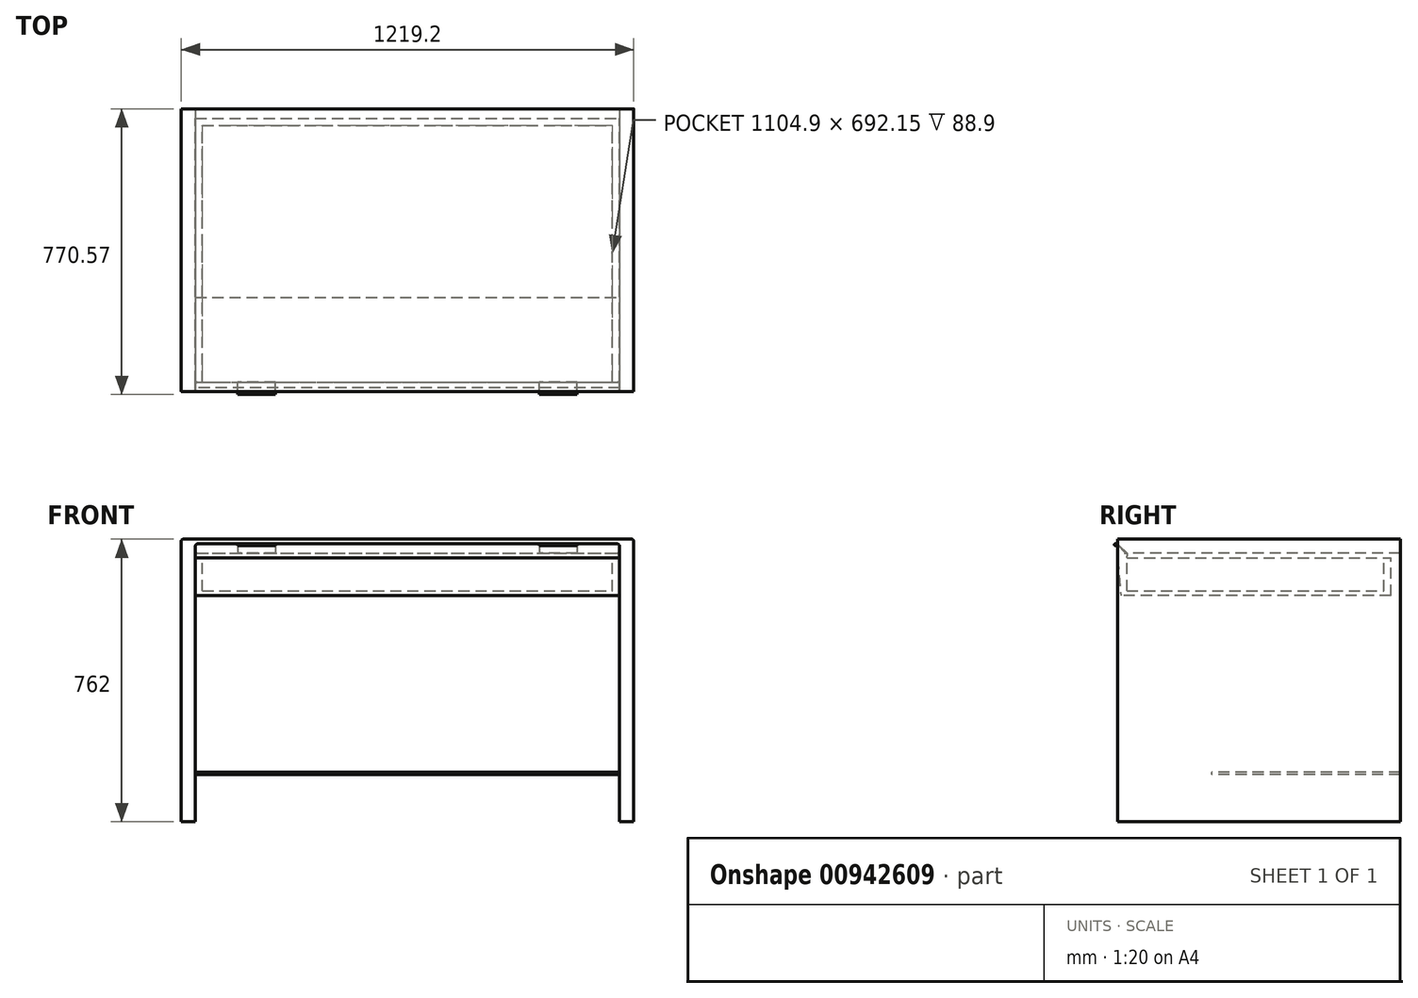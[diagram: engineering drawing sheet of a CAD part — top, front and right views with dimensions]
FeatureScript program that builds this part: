
annotation { "Feature Type Name" : "Feature", "Feature Type Description" : "" }
export const myFeature = defineFeature(function(context is Context, id is Id, definition is map)
    precondition{}
    {
        {
            var Q0;
            Q0=qCreatedBy(makeId("Top.planeOp"),FACE);
            var sketch = newSketch(context, id + "F0", { "sketchPlane" : qUnion([Q0])});
            skLineSegment(sketch, "E0.bottom", {"start": v(-1181.1, 736.46) * mm, "end": v(38.1, 736.46) * mm});
            skLineSegment(sketch, "E0.top", {"start": v(-1181.1, -25.54) * mm, "end": v(38.1, -25.54) * mm});
            skLineSegment(sketch, "E0.left", {"start": v(-1181.1, 736.46) * mm, "end": v(-1181.1, -25.54) * mm});
            skLineSegment(sketch, "E0.right", {"start": v(38.1, 736.46) * mm, "end": v(38.1, -25.54) * mm});
            skLineSegment(sketch, "E1", {"start": v(0, 736.46) * mm, "end": v(0, -25.54) * mm});
            skLineSegment(sketch, "E2", {"start": v(-1143, 736.46) * mm, "end": v(-1143, -25.54) * mm});
            skLineSegment(sketch, "E3", {"start": v(-1143, 228.46) * mm, "end": v(0, 228.46) * mm});
            skLineSegment(sketch, "E4", {"start": v(-1143, -0.14) * mm, "end": v(0, -0.14) * mm});
            skSolve(sketch);
        }
        {
            var Q0;
            {var subQ5=sQuery(id+"F0.wireOp",EDGE,"E4");Q0=makeQuery(id+"F0.imprint","IMPRINT",FACE,{"disambiguationData":[TD([[makeQuery(id+"F0.imprint","IMPRINT",EDGE,{"derivedFrom":subQ5}),-1.0]])]});}
            var Q1;
            {var subQ0=sQuery(id+"F0.wireOp",EDGE,"E3");Q1=makeQuery(id+"F0.imprint","IMPRINT",FACE,{"disambiguationData":[TD([[makeQuery(id+"F0.imprint","IMPRINT",EDGE,{"derivedFrom":subQ0}),-1.0]])]});}
            var Q2;
            {var subQ5=sQuery(id+"F0.wireOp",EDGE,"E3");Q2=makeQuery(id+"F0.imprint","IMPRINT",FACE,{"disambiguationData":[TD([[makeQuery(id+"F0.imprint","IMPRINT",EDGE,{"derivedFrom":subQ5}),1.0]])]});}
            extrude(context, id + "F1", {"entities" : qUnion([Q0, Q1, Q2]), "oppositeDirection" : true, "depth" : 38.1 * mm, "offsetDistance" : 25.4 * mm});
        }
        {
            var Q0;
            {var subQ4=sQuery(id+"F0.wireOp",EDGE,"E0.left");Q0=makeQuery(id+"F0.imprint","IMPRINT",FACE,{"disambiguationData":[TD([[makeQuery(id+"F0.imprint","IMPRINT",EDGE,{"derivedFrom":subQ4}),1.0]])]});}
            var Q1;
            {var subQ4=sQuery(id+"F0.wireOp",EDGE,"E0.right");Q1=makeQuery(id+"F0.imprint","IMPRINT",FACE,{"disambiguationData":[TD([[makeQuery(id+"F0.imprint","IMPRINT",EDGE,{"derivedFrom":subQ4}),-1.0]])]});}
            extrude(context, id + "F2", {"entities" : qUnion([Q0, Q1]), "operationType" : NewBodyOperationType.ADD, "oppositeDirection" : true, "depth" : 762 * mm, "offsetDistance" : 25.4 * mm});
        }
        {
            var Q0;
            Q0=makeQuery(id+"F1.opExtrude","CAP_EDGE",EDGE,{"disambiguationData":[OSD([sQuery(id+"F0.wireOp",EDGE,"E0.top")])],"isStart":false});
            chamfer(context, id + "F3", {"entities" : qUnion([Q0]), "width" : 25.4 * mm, "tangentPropagation" : true});
        }
        {
            var Q0;
            Q0=makeQuery(id+"F3.opChamfer","BLEND_EDGE",EDGE,{"blendedFrom":[makeQuery(id+"F1.opExtrude","CAP_EDGE",EDGE,{"disambiguationData":[OSD([sQuery(id+"F0.wireOp",EDGE,"E0.top")])],"isStart":false}),makeQuery(id+"F2.opExtrude","SWEPT_FACE",FACE,{"disambiguationData":[OSD([sQuery(id+"F0.wireOp",EDGE,"E2")])]})],"blendedInto":[makeQuery(id+"F2.opExtrude","SWEPT_FACE",FACE,{"disambiguationData":[OSD([sQuery(id+"F0.wireOp",EDGE,"E2")])]})]});
            var Q1;
            Q1=makeQuery(id+"F3.opChamfer","BLEND_EDGE",EDGE,{"blendedFrom":[makeQuery(id+"F1.opExtrude","CAP_EDGE",EDGE,{"disambiguationData":[OSD([sQuery(id+"F0.wireOp",EDGE,"E0.top")])],"isStart":false}),makeQuery(id+"F2.opExtrude","SWEPT_FACE",FACE,{"disambiguationData":[OSD([sQuery(id+"F0.wireOp",EDGE,"E1")])]})],"blendedInto":[makeQuery(id+"F2.opExtrude","SWEPT_FACE",FACE,{"disambiguationData":[OSD([sQuery(id+"F0.wireOp",EDGE,"E1")])]})]});
            fillet(context, id + "F4", {"entities" : qUnion([Q0, Q1]), "radius" : 5.08 * mm, "tangentPropagation" : true, "allowEdgeOverflow" : false});
        }
        {
            var Q0;
            {var subQ5=sQuery(id+"F0.wireOp",EDGE,"E4");Q0=makeQuery(id+"F0.imprint","IMPRINT",FACE,{"disambiguationData":[TD([[makeQuery(id+"F0.imprint","IMPRINT",EDGE,{"derivedFrom":subQ5}),-1.0]])]});}
            extrude(context, id + "F5", {"entities" : qUnion([Q0]), "oppositeDirection" : true, "depth" : 152.4 * mm, "offsetDistance" : 25.4 * mm, "hasSecondDirection" : true, "secondDirectionOppositeDirection" : true, "secondDirectionDepth" : 12.7 * mm});
        }
        {
            var Q0;
            Q0=makeQuery(id+"F5.opExtrude","CAP_EDGE",EDGE,{"disambiguationData":[OSD([sQuery(id+"F0.wireOp",EDGE,"E4")])],"isStart":true});
            chamfer(context, id + "F6", {"entities" : qUnion([Q0]), "width" : 25.4 * mm, "tangentPropagation" : true});
        }
        {
            var Q0;
            Q0=makeQuery(id+"F6.opChamfer","BLEND_EDGE",EDGE,{"blendedFrom":[makeQuery(id+"F5.opExtrude","CAP_EDGE",EDGE,{"disambiguationData":[OSD([sQuery(id+"F0.wireOp",EDGE,"E4")])],"isStart":true}),makeQuery(id+"F5.opExtrude","SWEPT_FACE",FACE,{"disambiguationData":[OSD([sQuery(id+"F0.wireOp",EDGE,"E2")])]})],"blendedInto":[makeQuery(id+"F5.opExtrude","SWEPT_FACE",FACE,{"disambiguationData":[OSD([sQuery(id+"F0.wireOp",EDGE,"E2")])]})]});
            var Q1;
            Q1=makeQuery(id+"F6.opChamfer","BLEND_EDGE",EDGE,{"blendedFrom":[makeQuery(id+"F5.opExtrude","CAP_EDGE",EDGE,{"disambiguationData":[OSD([sQuery(id+"F0.wireOp",EDGE,"E4")])],"isStart":true}),makeQuery(id+"F5.opExtrude","SWEPT_FACE",FACE,{"disambiguationData":[OSD([sQuery(id+"F0.wireOp",EDGE,"E1")])]})],"blendedInto":[makeQuery(id+"F5.opExtrude","SWEPT_FACE",FACE,{"disambiguationData":[OSD([sQuery(id+"F0.wireOp",EDGE,"E1")])]})]});
            fillet(context, id + "F7", {"entities" : qUnion([Q0, Q1]), "radius" : 5.08 * mm, "tangentPropagation" : true, "allowEdgeOverflow" : false});
        }
        {
            var Q0;
            {var subQ5=sQuery(id+"F0.wireOp",EDGE,"E3");Q0=makeQuery(id+"F0.imprint","IMPRINT",FACE,{"disambiguationData":[TD([[makeQuery(id+"F0.imprint","IMPRINT",EDGE,{"derivedFrom":subQ5}),1.0]])]});}
            extrude(context, id + "F8", {"entities" : qUnion([Q0]), "oppositeDirection" : true, "depth" : 635 * mm, "offsetDistance" : 25.4 * mm, "hasSecondDirection" : true, "secondDirectionOppositeDirection" : true, "secondDirectionDepth" : 628.65 * mm});
        }
        {
            var Q0;
            Q0=makeQuery(id+"F2.opExtrude","SWEPT_FACE",FACE,{"disambiguationData":[OSD([sQuery(id+"F0.wireOp",EDGE,"E0.left")])]});
            var sketch = newSketch(context, id + "F9", { "sketchPlane" : qUnion([Q0])});
            skLineSegment(sketch, "E5.bottom", {"start": v(6.49, -12.7) * mm, "end": v(31.89, -12.7) * mm});
            skLineSegment(sketch, "E5.top", {"start": v(6.49, -14.92) * mm, "end": v(31.89, -14.92) * mm});
            skLineSegment(sketch, "E5.left", {"start": v(6.49, -12.7) * mm, "end": v(6.49, -14.92) * mm});
            skLineSegment(sketch, "E5.right", {"start": v(31.89, -12.7) * mm, "end": v(31.89, -14.92) * mm});
            skArc(sketch, "E6", {"start": v(31.89, -12.7) * mm, "mid": v(33.46, -16.5) * mm, "end": v(29.67, -14.92) * mm});
            skLineSegment(sketch, "E7", {"start": v(25.54, -12.7) * mm, "end": v(0.14, -38.1) * mm});
            skLineSegment(sketch, "E8", {"start": v(25.54, -12.7) * mm, "end": v(25.54, -14.92) * mm});
            skLineSegment(sketch, "E9", {"start": v(25.54, -14.92) * mm, "end": v(2.36, -38.1) * mm});
            skLineSegment(sketch, "E10", {"start": v(0.14, -38.1) * mm, "end": v(2.36, -38.1) * mm});
            skSolve(sketch);
        }
        {
            var Q0;
            {var subQ0=sQuery(id+"F9.wireOp",EDGE,"E5.right");Q0=makeQuery(id+"F9.imprint","IMPRINT",FACE,{"disambiguationData":[TD([[makeQuery(id+"F9.imprint","IMPRINT",EDGE,{"derivedFrom":subQ0}),1.0]])]});}
            var Q1;
            {var subQ0=sQuery(id+"F9.wireOp",EDGE,"E5.right");Q1=makeQuery(id+"F9.imprint","IMPRINT",FACE,{"disambiguationData":[TD([[makeQuery(id+"F9.imprint","IMPRINT",EDGE,{"derivedFrom":subQ0}),-1.0]])]});}
            var Q2;
            {var subQ0=sQuery(id+"F9.wireOp",EDGE,"E9");Q2=makeQuery(id+"F9.imprint","IMPRINT",FACE,{"disambiguationData":[TD([[makeQuery(id+"F9.imprint","IMPRINT",EDGE,{"derivedFrom":subQ0}),-1.0]])]});}
            var Q3;
            {var subQ0=sQuery(id+"F9.wireOp",EDGE,"E8");Q3=makeQuery(id+"F9.imprint","IMPRINT",FACE,{"disambiguationData":[TD([[makeQuery(id+"F9.imprint","IMPRINT",EDGE,{"derivedFrom":subQ0}),1.0]])]});}
            extrude(context, id + "F10", {"entities" : qUnion([Q0, Q1, Q2, Q3]), "oppositeDirection" : true, "depth" : 254 * mm, "offsetDistance" : 25.4 * mm, "hasSecondDirection" : true, "secondDirectionOppositeDirection" : true, "secondDirectionDepth" : 152.4 * mm});
        }
        {
            var Q0;
            {var subQ0=sQuery(id+"F9.wireOp",EDGE,"E5.right");Q0=makeQuery(id+"F9.imprint","IMPRINT",FACE,{"disambiguationData":[TD([[makeQuery(id+"F9.imprint","IMPRINT",EDGE,{"derivedFrom":subQ0}),-1.0]])]});}
            var Q1;
            {var subQ0=sQuery(id+"F9.wireOp",EDGE,"E5.right");Q1=makeQuery(id+"F9.imprint","IMPRINT",FACE,{"disambiguationData":[TD([[makeQuery(id+"F9.imprint","IMPRINT",EDGE,{"derivedFrom":subQ0}),1.0]])]});}
            var Q2;
            {var subQ0=sQuery(id+"F9.wireOp",EDGE,"E9");Q2=makeQuery(id+"F9.imprint","IMPRINT",FACE,{"disambiguationData":[TD([[makeQuery(id+"F9.imprint","IMPRINT",EDGE,{"derivedFrom":subQ0}),-1.0]])]});}
            var Q3;
            {var subQ0=sQuery(id+"F9.wireOp",EDGE,"E8");Q3=makeQuery(id+"F9.imprint","IMPRINT",FACE,{"disambiguationData":[TD([[makeQuery(id+"F9.imprint","IMPRINT",EDGE,{"derivedFrom":subQ0}),1.0]])]});}
            extrude(context, id + "F11", {"entities" : qUnion([Q0, Q1, Q2, Q3]), "oppositeDirection" : true, "depth" : 1066.8 * mm, "offsetDistance" : 25.4 * mm, "hasSecondDirection" : true, "secondDirectionOppositeDirection" : true, "secondDirectionDepth" : 965.2 * mm});
        }
        {
            var Q0;
            Q0=makeQuery(id+"F2.opExtrude","CAP_EDGE",EDGE,{"disambiguationData":[OSD([sQuery(id+"F0.wireOp",EDGE,"E0.left")])],"isStart":true});
            fillet(context, id + "F12", {"entities" : qUnion([Q0]), "radius" : 5.08 * mm, "tangentPropagation" : true, "allowEdgeOverflow" : false});
        }
        {
            var Q0;
            Q0=makeQuery(id+"F2.opExtrude","CAP_EDGE",EDGE,{"disambiguationData":[OSD([sQuery(id+"F0.wireOp",EDGE,"E0.right")])],"isStart":true});
            fillet(context, id + "F13", {"entities" : qUnion([Q0]), "radius" : 5.08 * mm, "tangentPropagation" : true, "allowEdgeOverflow" : false});
        }
        {
            var Q0;
            {var subQ0=sQuery(id+"F0.wireOp",EDGE,"E1");var subQ1=sQuery(id+"F0.wireOp",EDGE,"E0.top");var subQ2=sQuery(id+"F0.wireOp",EDGE,"E0.bottom");var subQ3=sQuery(id+"F0.wireOp",EDGE,"E2");Q0=makeQuery(id+"F2.boolean.opBoolean","MERGE",FACE,{"derivedFrom":[makeQuery(id+"F1.opExtrude","CAP_FACE",FACE,{"disambiguationData":[OSD([subQ2,subQ1,subQ0,subQ3])],"isStart":true}),makeQuery(id+"F2.opExtrude","CAP_FACE",FACE,{"disambiguationData":[OSD([subQ2,subQ1,sQuery(id+"F0.wireOp",EDGE,"E0.left"),subQ3])],"isStart":true}),makeQuery(id+"F2.opExtrude","CAP_FACE",FACE,{"disambiguationData":[OSD([subQ2,subQ1,sQuery(id+"F0.wireOp",EDGE,"E0.right"),subQ0])],"isStart":true})]});}
            var sketch = newSketch(context, id + "F14", { "sketchPlane" : qUnion([Q0])});
            skLineSegment(sketch, "E11.bottom", {"start": v(-1143, -25.54) * mm, "end": v(0, -25.54) * mm});
            skLineSegment(sketch, "E11.top", {"start": v(-1143, 736.46) * mm, "end": v(0, 736.46) * mm});
            skLineSegment(sketch, "E11.left", {"start": v(-1143, -25.54) * mm, "end": v(-1143, 736.46) * mm});
            skLineSegment(sketch, "E11.right", {"start": v(0, -25.54) * mm, "end": v(0, 736.46) * mm});
            skLineSegment(sketch, "E12", {"start": v(-1143, -0.14) * mm, "end": v(0, -0.14) * mm});
            skLineSegment(sketch, "E13", {"start": v(-19.05, -0.14) * mm, "end": v(-19.05, 736.46) * mm});
            skLineSegment(sketch, "E14", {"start": v(-1123.95, -0.14) * mm, "end": v(-1123.95, 736.46) * mm});
            skLineSegment(sketch, "E15", {"start": v(-1143, 711.06) * mm, "end": v(0, 711.06) * mm});
            skLineSegment(sketch, "E16", {"start": v(-1143, 692.01) * mm, "end": v(0, 692.01) * mm});
            skSolve(sketch);
        }
        {
            var Q0;
            {var subQ0=sQuery(id+"F14.wireOp",EDGE,"E12");var subQ1=sQuery(id+"F14.wireOp",EDGE,"E11.left");var subQ2=makeQuery(id+"F14.imprint","INTERSECT",VERTEX,{"derivedFrom":[subQ1,subQ0]});Q0=makeQuery(id+"F14.imprint","IMPRINT",FACE,{"disambiguationData":[TD([[makeQuery(id+"F14.imprint","IMPRINT",EDGE,{"disambiguationData":[TD([[subQ2,-1.0]])],"derivedFrom":subQ1}),-1.0]])]});}
            var Q1;
            {var subQ0=sQuery(id+"F14.wireOp",EDGE,"E12");var subQ1=sQuery(id+"F14.wireOp",EDGE,"E11.right");var subQ2=makeQuery(id+"F14.imprint","INTERSECT",VERTEX,{"derivedFrom":[subQ1,subQ0]});Q1=makeQuery(id+"F14.imprint","IMPRINT",FACE,{"disambiguationData":[TD([[makeQuery(id+"F14.imprint","IMPRINT",EDGE,{"disambiguationData":[TD([[subQ2,-1.0]])],"derivedFrom":subQ1}),1.0]])]});}
            var Q2;
            {var subQ0=sQuery(id+"F14.wireOp",EDGE,"E16");var subQ1=sQuery(id+"F14.wireOp",EDGE,"E13");var subQ2=makeQuery(id+"F14.imprint","INTERSECT",VERTEX,{"derivedFrom":[subQ1,subQ0]});Q2=makeQuery(id+"F14.imprint","IMPRINT",FACE,{"disambiguationData":[TD([[makeQuery(id+"F14.imprint","IMPRINT",EDGE,{"disambiguationData":[TD([[subQ2,-1.0]])],"derivedFrom":subQ1}),1.0]])]});}
            var Q3;
            {var subQ0=sQuery(id+"F14.wireOp",EDGE,"E15");var subQ1=sQuery(id+"F14.wireOp",EDGE,"E11.right");var subQ2=makeQuery(id+"F14.imprint","INTERSECT",VERTEX,{"derivedFrom":[subQ1,subQ0]});Q3=makeQuery(id+"F14.imprint","IMPRINT",FACE,{"disambiguationData":[TD([[makeQuery(id+"F14.imprint","IMPRINT",EDGE,{"disambiguationData":[TD([[subQ2,1.0]])],"derivedFrom":subQ1}),1.0]])]});}
            var Q4;
            {var subQ0=sQuery(id+"F14.wireOp",EDGE,"E15");var subQ1=sQuery(id+"F14.wireOp",EDGE,"E11.left");var subQ2=makeQuery(id+"F14.imprint","INTERSECT",VERTEX,{"derivedFrom":[subQ1,subQ0]});Q4=makeQuery(id+"F14.imprint","IMPRINT",FACE,{"disambiguationData":[TD([[makeQuery(id+"F14.imprint","IMPRINT",EDGE,{"disambiguationData":[TD([[subQ2,1.0]])],"derivedFrom":subQ1}),-1.0]])]});}
            extrude(context, id + "F15", {"entities" : qUnion([Q0, Q1, Q2, Q3, Q4]), "oppositeDirection" : true, "depth" : 152.4 * mm, "offsetDistance" : 25.4 * mm, "hasSecondDirection" : true, "secondDirectionOppositeDirection" : true, "secondDirectionDepth" : 50.8 * mm});
        }
        {
            var Q0;
            {var subQ0=sQuery(id+"F14.wireOp",EDGE,"E13");var subQ1=sQuery(id+"F14.wireOp",EDGE,"E12");var subQ2=makeQuery(id+"F14.imprint","INTERSECT",VERTEX,{"derivedFrom":[subQ1,subQ0]});Q0=makeQuery(id+"F14.imprint","IMPRINT",FACE,{"disambiguationData":[TD([[makeQuery(id+"F14.imprint","IMPRINT",EDGE,{"disambiguationData":[TD([[subQ2,1.0]])],"derivedFrom":subQ1}),1.0]])]});}
            extrude(context, id + "F16", {"entities" : qUnion([Q0]), "operationType" : NewBodyOperationType.ADD, "oppositeDirection" : true, "depth" : 152.4 * mm, "offsetDistance" : 25.4 * mm, "hasSecondDirection" : true, "secondDirectionOppositeDirection" : true, "secondDirectionDepth" : 139.7 * mm});
        }
        {
            var Q0;
            Q0=makeQuery(id+"F5.opExtrude","CAP_EDGE",EDGE,{"disambiguationData":[OSD([sQuery(id+"F0.wireOp",EDGE,"E0.top")])],"isStart":false});
            chamfer(context, id + "F17", {"entities" : qUnion([Q0]), "chamferType" : ChamferType.TWO_OFFSETS, "width1" : 101.6 * mm, "oppositeDirection" : false, "width2" : 9.52 * mm, "tangentPropagation" : true});
        }
    });
